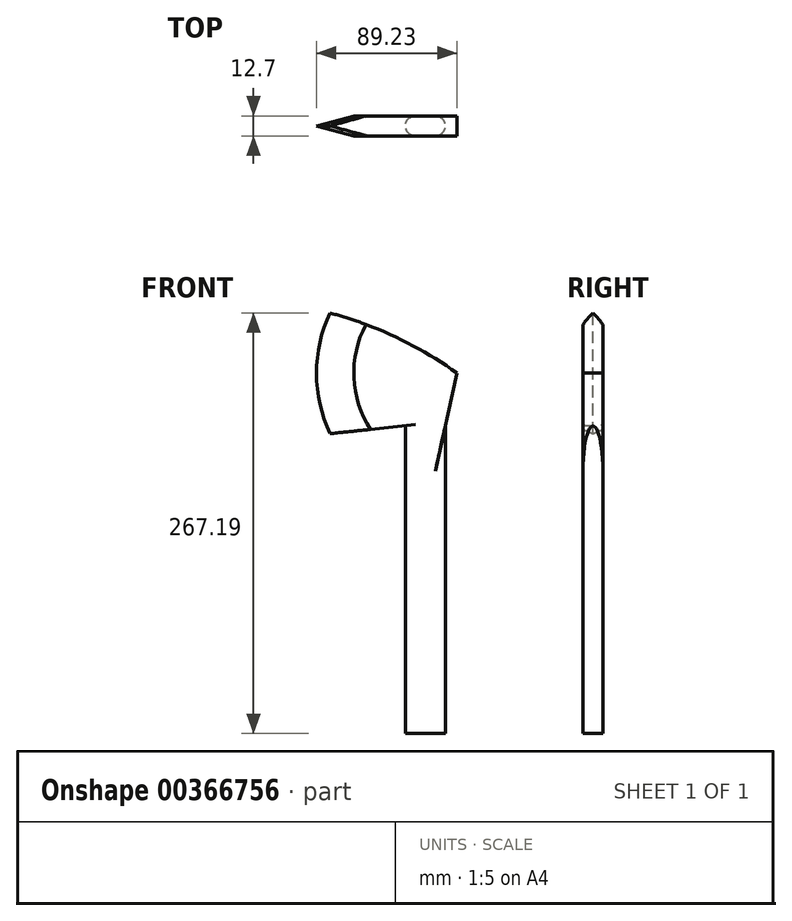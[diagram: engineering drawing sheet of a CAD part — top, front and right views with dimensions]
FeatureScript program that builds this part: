
annotation { "Feature Type Name" : "Feature", "Feature Type Description" : "" }
export const myFeature = defineFeature(function(context is Context, id is Id, definition is map)
    precondition{}
    {
        {
            var Q0;
            Q0=qCreatedBy(makeId("Front.planeOp"),FACE);
            var sketch = newSketch(context, id + "F0", { "sketchPlane" : qUnion([Q0])});
            skLineSegment(sketch, "E0", {"start": v(-12.7, -99.27) * mm, "end": v(-12.7, -35.77) * mm});
            skLineSegment(sketch, "E1", {"start": v(-12.7, -30.69) * mm, "end": v(-12.7, 32.81) * mm});
            skLineSegment(sketch, "E2.MirrorCS", {"start": v(12.7, -30.69) * mm, "end": v(12.7, 32.81) * mm});
            skLineSegment(sketch, "E3.MirrorCS", {"start": v(12.7, -99.27) * mm, "end": v(12.7, -35.77) * mm});
            skArc(sketch, "E4", {"start": v(-62.22, 104.86) * mm, "mid": v(-70.84, 66.23) * mm, "end": v(-62.22, 27.6) * mm});
            skLineSegment(sketch, "E5", {"start": v(20.1, 66.23) * mm, "end": v(12.7, 32.81) * mm});
            skArc(sketch, "E6", {"start": v(20.1, 66.23) * mm, "mid": v(-19.28, 89.34) * mm, "end": v(-62.22, 104.86) * mm});
            skLineSegment(sketch, "E7", {"start": v(12.7, -30.69) * mm, "end": v(12.7, -35.77) * mm});
            skLineSegment(sketch, "E8", {"start": v(-12.7, -30.69) * mm, "end": v(-12.7, -35.77) * mm});
            skLineSegment(sketch, "E9", {"start": v(-12.7, 32.81) * mm, "end": v(-62.22, 27.6) * mm});
            skLineSegment(sketch, "E10", {"start": v(-12.7, -99.27) * mm, "end": v(-12.7, -162.77) * mm});
            skLineSegment(sketch, "E11.MirrorCS", {"start": v(12.7, -99.27) * mm, "end": v(12.7, -162.77) * mm});
            skLineSegment(sketch, "E12", {"start": v(-12.7, -162.77) * mm, "end": v(12.7, -162.77) * mm});
            skSolve(sketch);
        }
        {
            var Q0;
            Q0=qSketchRegion(id+"F0",true);
            extrude(context, id + "F1", {"entities" : qUnion([Q0]), "depth" : 12.7 * mm});
        }
        {
            var Q0;
            Q0=makeQuery(id+"F1.opExtrude","CAP_EDGE",EDGE,{"disambiguationData":[OSD([sQuery(id+"F0.wireOp",EDGE,"E2.MirrorCS"),sQuery(id+"F0.wireOp",EDGE,"E3.MirrorCS"),sQuery(id+"F0.wireOp",EDGE,"E7")])],"isStart":false});
            var Q1;
            Q1=makeQuery(id+"F1.opExtrude","CAP_EDGE",EDGE,{"disambiguationData":[OSD([sQuery(id+"F0.wireOp",EDGE,"E2.MirrorCS"),sQuery(id+"F0.wireOp",EDGE,"E3.MirrorCS"),sQuery(id+"F0.wireOp",EDGE,"E7")])],"isStart":true});
            var Q2;
            Q2=makeQuery(id+"F1.opExtrude","CAP_EDGE",EDGE,{"disambiguationData":[OSD([sQuery(id+"F0.wireOp",EDGE,"E0"),sQuery(id+"F0.wireOp",EDGE,"E1"),sQuery(id+"F0.wireOp",EDGE,"E8")])],"isStart":true});
            var Q3;
            Q3=makeQuery(id+"F1.opExtrude","CAP_EDGE",EDGE,{"disambiguationData":[OSD([sQuery(id+"F0.wireOp",EDGE,"E0"),sQuery(id+"F0.wireOp",EDGE,"E1"),sQuery(id+"F0.wireOp",EDGE,"E8")])],"isStart":false});
            fillet(context, id + "F2", {"entities" : qUnion([Q0, Q1, Q2, Q3]), "radius" : 6.35 * mm, "tangentPropagation" : true, "allowEdgeOverflow" : false});
        }
        {
            var Q0;
            Q0=makeQuery(id+"F1.opExtrude","CAP_EDGE",EDGE,{"disambiguationData":[OSD([sQuery(id+"F0.wireOp",EDGE,"E4")])],"isStart":false});
            var Q1;
            Q1=makeQuery(id+"F1.opExtrude","CAP_EDGE",EDGE,{"disambiguationData":[OSD([sQuery(id+"F0.wireOp",EDGE,"E4")])],"isStart":true});
            chamfer(context, id + "F3", {"entities" : qUnion([Q0, Q1]), "chamferType" : ChamferType.OFFSET_ANGLE, "width" : 25.4 * mm, "oppositeDirection" : false, "angle" : 15 * degree, "tangentPropagation" : true});
        }
    });
